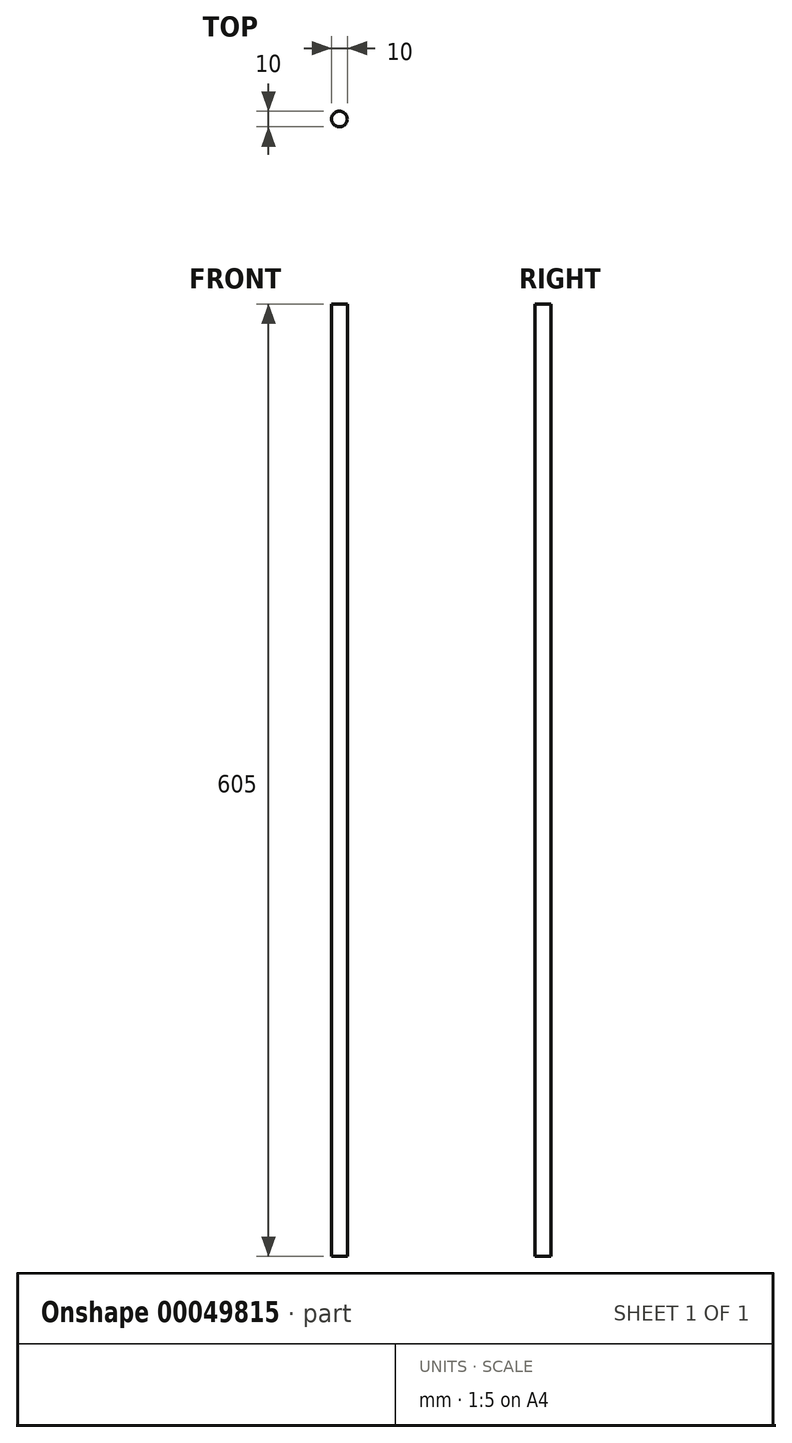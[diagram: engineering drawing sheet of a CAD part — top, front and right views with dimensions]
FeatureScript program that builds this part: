
annotation { "Feature Type Name" : "Feature", "Feature Type Description" : "" }
export const myFeature = defineFeature(function(context is Context, id is Id, definition is map)
    precondition{}
    {
        {
            var Q0;
            Q0=qCreatedBy(makeId("Top.planeOp"),FACE);
            var sketch = newSketch(context, id + "F0", { "sketchPlane" : qUnion([Q0])});
            skCircle(sketch, "E0", {"center": v(0, 0) * mm, "radius": 5 * mm});
            skSolve(sketch);
        }
        {
            var Q0;
            Q0=qSketchRegion(id+"F0",true);
            extrude(context, id + "F1", {"entities" : qUnion([Q0]), "depth" : 605 * mm});
        }
    });
